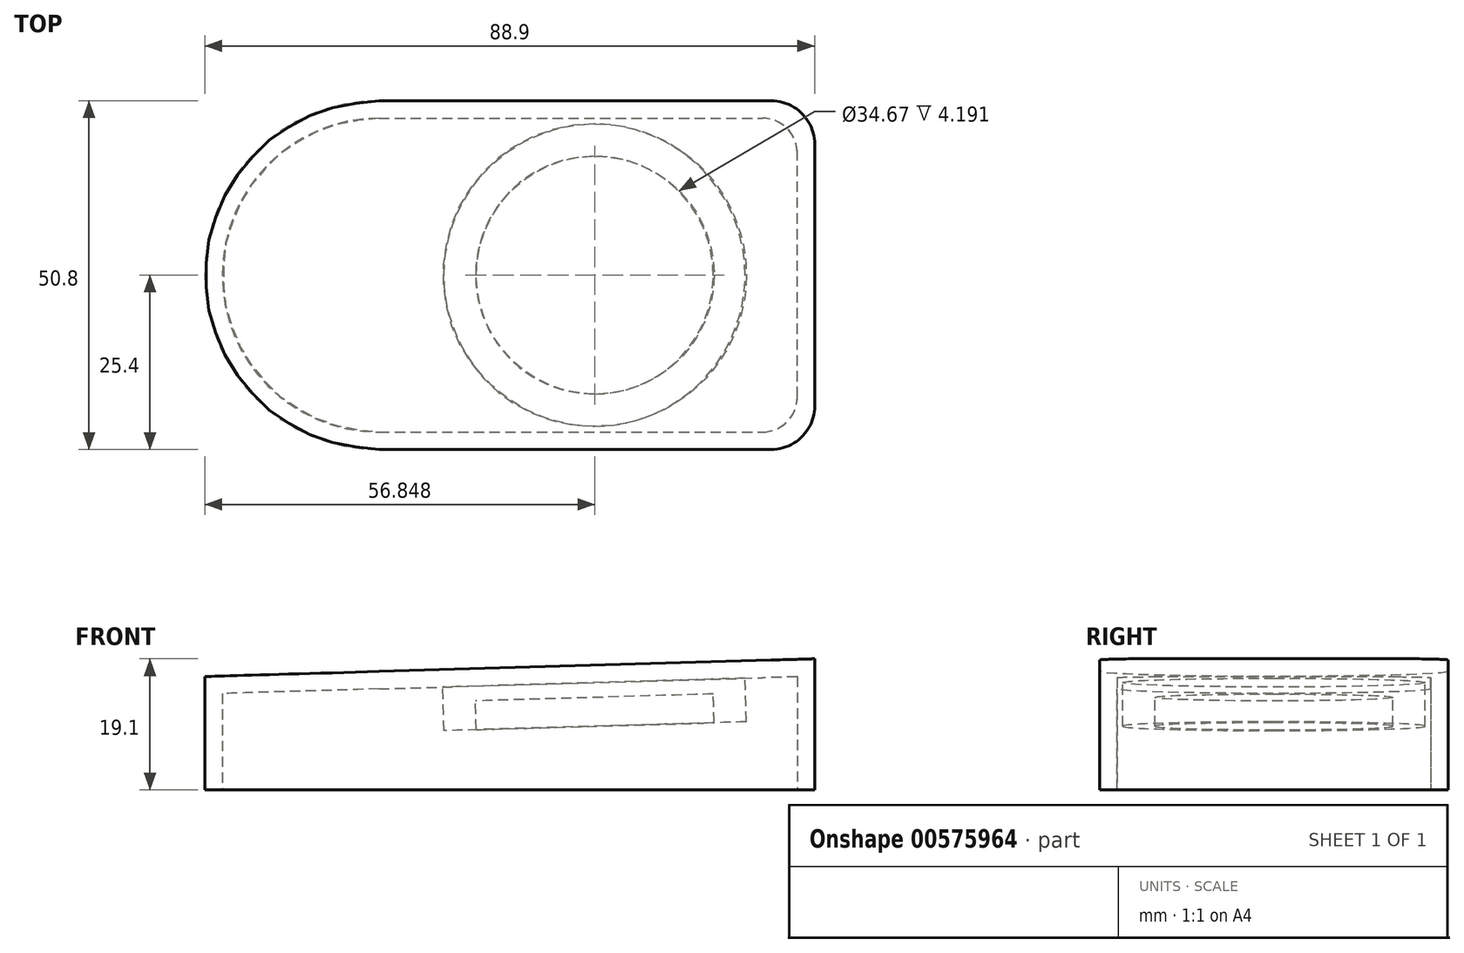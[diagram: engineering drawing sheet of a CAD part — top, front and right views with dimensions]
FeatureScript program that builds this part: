
annotation { "Feature Type Name" : "Feature", "Feature Type Description" : "" }
export const myFeature = defineFeature(function(context is Context, id is Id, definition is map)
    precondition{}
    {
        {
            var Q0;
            Q0=qCreatedBy(makeId("Top.planeOp"),FACE);
            var sketch = newSketch(context, id + "F0", { "sketchPlane" : qUnion([Q0])});
            skLineSegment(sketch, "E0.bottom", {"start": v(-50.78, 0) * mm, "end": v(12.72, 0) * mm});
            skLineSegment(sketch, "E0.top", {"start": v(-50.78, 50.8) * mm, "end": v(12.72, 50.8) * mm});
            skLineSegment(sketch, "E0.right", {"start": v(12.72, 0) * mm, "end": v(12.72, 50.8) * mm});
            skArc(sketch, "E1", {"start": v(-50.78, 50.8) * mm, "mid": v(-76.18, 25.4) * mm, "end": v(-50.78, 0) * mm});
            skSolve(sketch);
        }
        {
            var Q0;
            Q0 = qSketchRegion(id + "F0", true);
            extrude(context, id + "F1", {"entities" : qUnion([Q0]), "depth" : 19.1 * mm, "offsetDistance" : 25.4 * mm});
        }
        {
            var Q0;
            Q0=makeQuery(id+"F1.opExtrude","SWEPT_FACE",FACE,{"disambiguationData":[OSD([sQuery(id+"F0.wireOp",EDGE,"E0.bottom")])]});
            var sketch = newSketch(context, id + "F2", { "sketchPlane" : qUnion([Q0])});
            skLineSegment(sketch, "E2", {"start": v(12.72, 19.1) * mm, "end": v(-76.18, 16.51) * mm});
            skLineSegment(sketch, "E3", {"start": v(-76.18, 16.5) * mm, "end": v(-76.18, 19.1) * mm});
            skLineSegment(sketch, "E4", {"start": v(-76.18, 19.1) * mm, "end": v(12.72, 19.1) * mm});
            skSolve(sketch);
        }
        {
            var Q0;
            Q0 = qSketchRegion(id + "F2", true);
            extrude(context, id + "F3", {"entities" : qUnion([Q0]), "operationType" : NewBodyOperationType.REMOVE, "oppositeDirection" : true, "depth" : 76.2 * mm, "offsetDistance" : 25.4 * mm});
        }
        {
            var Q0;
            Q0=makeQuery(id+"F1.opExtrude","CAP_FACE",FACE,{"disambiguationData":[OSD([sQuery(id+"F0.wireOp",EDGE,"E0.bottom"),sQuery(id+"F0.wireOp",EDGE,"E0.top"),sQuery(id+"F0.wireOp",EDGE,"E0.right"),sQuery(id+"F0.wireOp",EDGE,"E1")])],"isStart":true});
            shell(context, id + "F4", {"entities" : qUnion([Q0]), "thickness" : 2.54 * mm});
        }
        {
            var Q0;
            Q0=makeQuery(id+"F4.opShell","OFFSET_FACE",FACE,{"disambiguationData":[OSD([sQuery(id+"F2.wireOp",EDGE,"E2")])]});
            var sketch = newSketch(context, id + "F5", { "sketchPlane" : qUnion([Q0])});
            skCircle(sketch, "E5", {"center": v(-19, -25.4) * mm, "radius": 22.03 * mm});
            skPoint(sketch, "E5.centerSnap0", {"position": v(-27.46, -25.4) * mm});
            skSolve(sketch);
        }
        {
            var Q0;
            Q0 = qSketchRegion(id + "F5", true);
            extrude(context, id + "F6", {"entities" : qUnion([Q0]), "operationType" : NewBodyOperationType.ADD, "depth" : 6.35 * mm, "offsetDistance" : 25.4 * mm});
        }
        {
            var Q0;
            Q0=makeQuery(id+"F1.opExtrude","SWEPT_EDGE",EDGE,{"disambiguationData":[OSD([sQuery(id+"F0.wireOp",EDGE,"E0.top"),sQuery(id+"F0.wireOp",EDGE,"E0.right")])]});
            var Q1;
            Q1=makeQuery(id+"F1.opExtrude","SWEPT_EDGE",EDGE,{"disambiguationData":[OSD([sQuery(id+"F0.wireOp",EDGE,"E0.bottom"),sQuery(id+"F0.wireOp",EDGE,"E0.right")])]});
            fillet(context, id + "F7", {"entities" : qUnion([Q0, Q1]), "radius" : 6.35 * mm, "tangentPropagation" : true, "allowEdgeOverflow" : false});
        }
        {
            var Q0;
            Q0=makeQuery(id+"F6.opExtrude","CAP_FACE",FACE,{"disambiguationData":[OSD([sQuery(id+"F5.wireOp",EDGE,"E5")])],"isStart":false});
            shell(context, id + "F8", {"entities" : qUnion([Q0]), "thickness" : 4.7 * mm});
        }
        {
            var Q0;
            Q0=makeQuery(id+"F4.opShell","OFFSET_EDGE",EDGE,{"disambiguationData":[OSD([sQuery(id+"F0.wireOp",EDGE,"E0.bottom"),sQuery(id+"F0.wireOp",EDGE,"E0.right")])]});
            var Q1;
            Q1=makeQuery(id+"F4.opShell","OFFSET_EDGE",EDGE,{"disambiguationData":[OSD([sQuery(id+"F0.wireOp",EDGE,"E0.top"),sQuery(id+"F0.wireOp",EDGE,"E0.right")])]});
            fillet(context, id + "F9", {"entities" : qUnion([Q0, Q1]), "radius" : 5.08 * mm, "tangentPropagation" : true, "allowEdgeOverflow" : false});
        }
    });
